# Revit family: KEUCO_14921010000
name_source: partatom
category: Sonderausstattung
revit_build: Autodesk Revit 2016 (Build: 20150220_1215(x64)
units: mm (PartAtom-declared; Revit-internal decimal feet)

## family parameters
Arbeitsebenenbasiert = Nein
Beim Laden mit Abzugskörper schneiden = Nein
Bemaßung runder Anschluss = Durchmesser verwenden
Gemeinsam genutzt = Nein
Immer vertikal = Ja
Raumberechnungspunkt = Nein
Teiletyp = Normal

## types (3) — shared parameters
Beschreibung = --
Breite = 226 mm  [stored 0.74147 ft]
Gewicht = 382
Hersteller = KEUCO
Kategorie = ACC
Preisgruppe = 1
Serie = Plan
URL = https://www.keuco.com
Verwendung = GWC / WC

## per-type parameters (varying)
| type | Ausschreibungstext |
| 14921010000 | KEUCO PLAN Handtuchring 14921010000
Hochglanzverchromter Handtuchring 
in ästhetischem, funktionalem Design, 
geschlossene, rechteckige Form
Ring schwenkbar, antistatisch, leicht zu reinigen
Breite 226 mm, Höhe 132 mm
Der Handtuchring wird verdeckt angebracht
Lieferung inkl. korrosionsfreiem Befestigungsmaterial |
| 14921070000 | KEUCO PLAN Handtuchring 14921070000
Handtuchring aus hochwertigem Edelstahl 
in ästhetischem, funktionalem Design,
geschlossene, rechteckige Form
Ring schwenkbar, antistatisch, leicht zu reinigen
Breite 226 mm, Höhe 132 mm
Der Handtuchring wird verdeckt angebracht
Lieferung inkl. korrosionsfreiem Befestigungsmaterial |
| 14921170000 | KEUCO PLAN Handtuchring 14921170000
Handtuchhalter aus 
silber-eloxiertem Aluminium (E6 EV1)/verchromt 
in ästhetischem, funktionalem Design
geschlossene, rechteckige Form
Ring schwenkbar, antistatisch, leicht zu reinigen
Die Wandhalterung ist als Design-Element hochglanzverchromt
Breite 226 mm, Höhe 132 mm
Der Handtuchring wird verdeckt angebracht
Lieferung inkl. korrosionsfreiem Befestigungsmaterial |

note: column(s) folded — value = type name in every type: Artikelnummer

note: [stored X ft] marks values corroborated as IEEE doubles in the binary element streams (Revit-internal decimal feet)

## geometry (parser evidence)
native form markers: Blend x4, Sweep x2
no freeform markers — native parametric forms only
